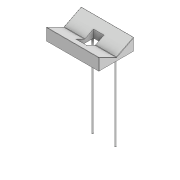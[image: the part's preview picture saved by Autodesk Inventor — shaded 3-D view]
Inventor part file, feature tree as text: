
AUTODESK INVENTOR PART (.ipt)
format: ipt  version: 2020 (Build 240168000, 168)  size: 137,728 bytes
history: native  units: mm
features: extrude x4, sketch x4, chamfer x1
ambient origin geometry x8: Origin, YZ Plane, XZ Plane, XY Plane, X Axis, Y Axis, Z Axis, Center Point
bodies: Volumenkörper1 (feature_tree)
feature tree (9):
  extrude  "Extrusion1"  Depth=200.0mm
  extrude  "Extrusion2"  Depth=10.0mm
  extrude  "Extrusion3"  Depth=200.0mm
  chamfer  "Fase2"  Distance=20.0mm
  extrude  "Extrusion4"  Depth=500.0mm TaperAngle=0.0deg
  sketch  "Skizze1"  dims[d0=300.0mm d1=200.0mm]
  sketch  "Skizze2"  dims[d2=20.0mm d3=0.0mm d5=10.0mm]
  sketch  "Skizze5"  dims[d6=200.0mm d7=20.0mm]
  sketch  "Skizze6"  dims[d8=10.0mm d9=20.0mm d11=500.0mm d12=0.0mm d17=70.0mm d18=70.0mm d19=113.5mm d20=0.0mm d21=2.0mm d22=2.0mm d23=45.0deg d24=60.0mm d25=100.0mm d26=0.0mm d27=0.0mm d28=65.0mm d29=65.0mm]
